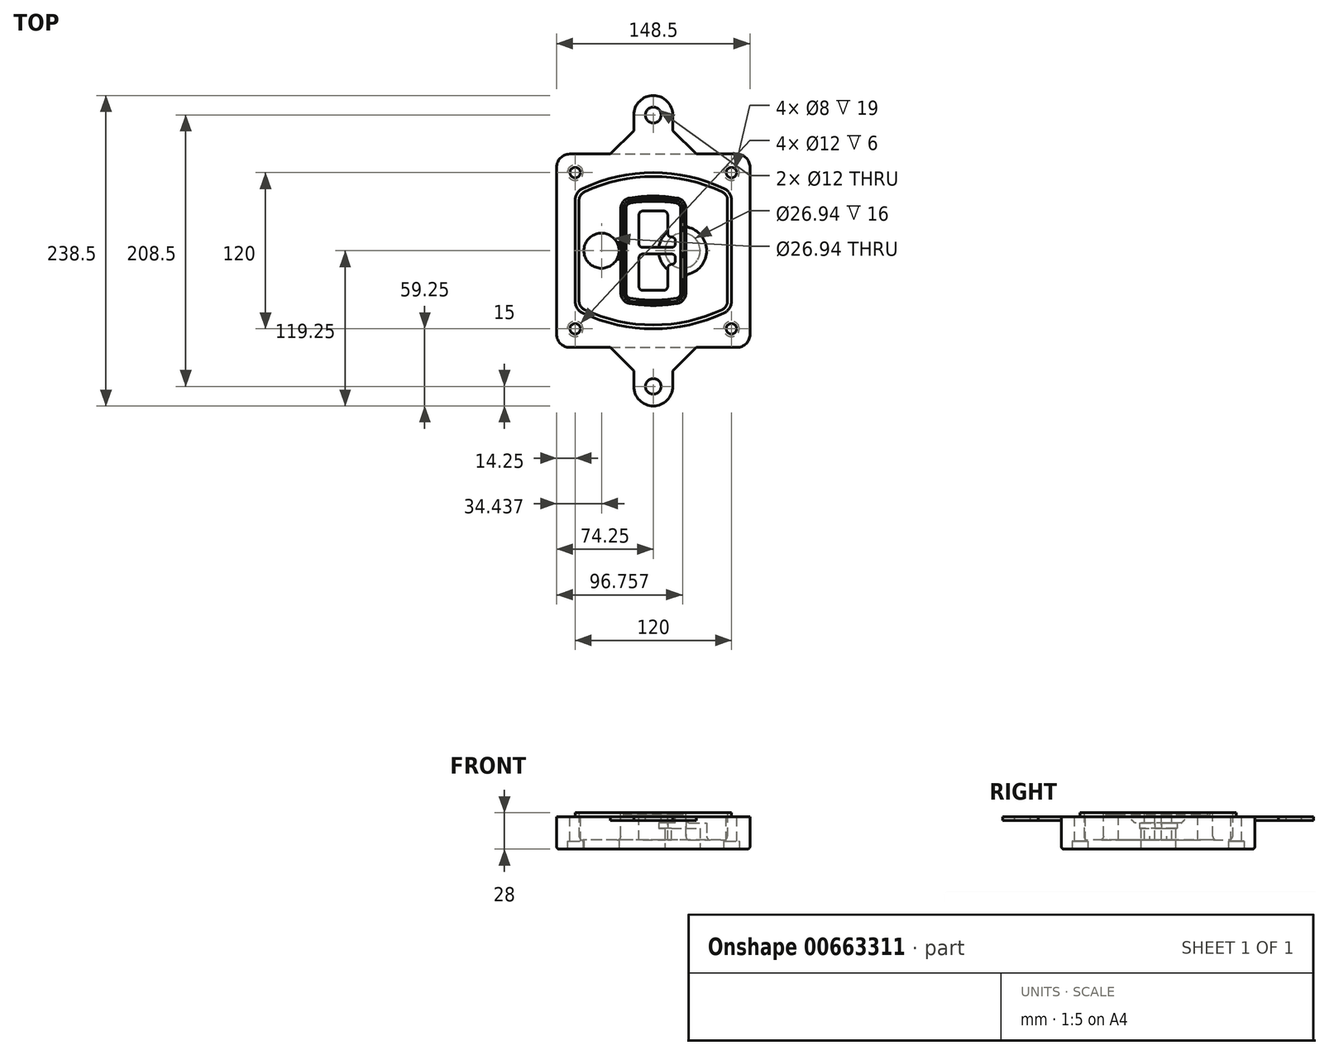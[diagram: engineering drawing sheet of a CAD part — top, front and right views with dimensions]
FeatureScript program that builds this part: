
annotation { "Feature Type Name" : "Feature", "Feature Type Description" : "" }
export const myFeature = defineFeature(function(context is Context, id is Id, definition is map)
    precondition{}
    {
        {
            var Q0;
            Q0=qCreatedBy(makeId("Top.planeOp"),FACE);
            var sketch = newSketch(context, id + "F0", { "sketchPlane" : qUnion([Q0])});
            skPoint(sketch, "E0.rect.middle", {"position": v(0, 0) * mm});
            skLineSegment(sketch, "E1.bottom", {"start": v(-64.25, -74.25) * mm, "end": v(64.25, -74.25) * mm});
            skLineSegment(sketch, "E1.top", {"start": v(-64.25, 74.25) * mm, "end": v(64.25, 74.25) * mm});
            skLineSegment(sketch, "E1.left", {"start": v(-74.25, -64.25) * mm, "end": v(-74.25, 64.25) * mm});
            skLineSegment(sketch, "E1.right", {"start": v(74.25, -64.25) * mm, "end": v(74.25, 64.25) * mm});
            skLineSegment(sketch, "E2", {"start": v(-74.25, 74.25) * mm, "end": v(74.25, -74.25) * mm, "construction": true});
            skLineSegment(sketch, "E3", {"start": v(74.25, 74.25) * mm, "end": v(-74.25, -74.25) * mm, "construction": true});
            skCircle(sketch, "E4", {"center": v(-60, 60) * mm, "radius": 4 * mm});
            skCircle(sketch, "E5", {"center": v(60, 60) * mm, "radius": 4 * mm});
            skCircle(sketch, "E6", {"center": v(60, -60) * mm, "radius": 4 * mm});
            skCircle(sketch, "E7", {"center": v(-60, -60) * mm, "radius": 4 * mm});
            skLineSegment(sketch, "E8", {"start": v(-60, 60) * mm, "end": v(60, 60) * mm, "construction": true});
            skLineSegment(sketch, "E9", {"start": v(60, 60) * mm, "end": v(60, -60) * mm, "construction": true});
            skLineSegment(sketch, "E10", {"start": v(60, -60) * mm, "end": v(-60, -60) * mm, "construction": true});
            skLineSegment(sketch, "E11", {"start": v(-60, -60) * mm, "end": v(-60, 60) * mm, "construction": true});
            skLineSegment(sketch, "E12", {"start": v(-60, 38.83) * mm, "end": v(-60, -38.83) * mm});
            skLineSegment(sketch, "E13", {"start": v(60, 38.83) * mm, "end": v(60, -38.83) * mm});
            skArc(sketch, "E14", {"start": v(54.26, 47.88) * mm, "mid": v(0, 60) * mm, "end": v(-54.26, 47.88) * mm});
            skArc(sketch, "E15", {"start": v(-54.26, -47.88) * mm, "mid": v(0, -60) * mm, "end": v(54.26, -47.88) * mm});
            skLineSegment(sketch, "E16", {"start": v(-60, 0) * mm, "end": v(60, 0) * mm, "construction": true});
            skPoint(sketch, "E17.visualSharp", {"position": v(-60, -45) * mm});
            skArc(sketch, "E17.filletArc", {"start": v(-60, -38.83) * mm, "mid": v(-58.44, -44.2) * mm, "end": v(-54.26, -47.88) * mm});
            skPoint(sketch, "E18.visualSharp", {"position": v(-60, 45) * mm});
            skArc(sketch, "E18.filletArc", {"start": v(-54.26, 47.88) * mm, "mid": v(-58.44, 44.2) * mm, "end": v(-60, 38.83) * mm});
            skPoint(sketch, "E19.visualSharp", {"position": v(60, 45) * mm});
            skArc(sketch, "E19.filletArc", {"start": v(60, 38.83) * mm, "mid": v(58.44, 44.2) * mm, "end": v(54.26, 47.88) * mm});
            skPoint(sketch, "E20.visualSharp", {"position": v(60, -45) * mm});
            skArc(sketch, "E20.filletArc", {"start": v(54.26, -47.88) * mm, "mid": v(58.44, -44.2) * mm, "end": v(60, -38.83) * mm});
            skPoint(sketch, "E21.visualSharp", {"position": v(-74.25, 74.25) * mm});
            skArc(sketch, "E21.filletArc", {"start": v(-64.25, 74.25) * mm, "mid": v(-71.32, 71.32) * mm, "end": v(-74.25, 64.25) * mm});
            skPoint(sketch, "E22.visualSharp", {"position": v(74.25, 74.25) * mm});
            skArc(sketch, "E22.filletArc", {"start": v(74.25, 64.25) * mm, "mid": v(71.32, 71.32) * mm, "end": v(64.25, 74.25) * mm});
            skPoint(sketch, "E23.visualSharp", {"position": v(74.25, -74.25) * mm});
            skArc(sketch, "E23.filletArc", {"start": v(64.25, -74.25) * mm, "mid": v(71.32, -71.32) * mm, "end": v(74.25, -64.25) * mm});
            skPoint(sketch, "E24.visualSharp", {"position": v(-74.25, -74.25) * mm});
            skArc(sketch, "E24.filletArc", {"start": v(-74.25, -64.25) * mm, "mid": v(-71.32, -71.32) * mm, "end": v(-64.25, -74.25) * mm});
            skArc(sketch, "E25.0", {"start": v(57, 38.83) * mm, "mid": v(55.9, 42.58) * mm, "end": v(52.98, 45.17) * mm});
            skLineSegment(sketch, "E25.1", {"start": v(57, 38.83) * mm, "end": v(57, -38.83) * mm});
            skArc(sketch, "E25.2", {"start": v(52.98, -45.17) * mm, "mid": v(55.9, -42.58) * mm, "end": v(57, -38.83) * mm});
            skArc(sketch, "E25.3", {"start": v(-52.98, -45.17) * mm, "mid": v(0, -57) * mm, "end": v(52.98, -45.17) * mm});
            skArc(sketch, "E25.4", {"start": v(-57, -38.83) * mm, "mid": v(-55.9, -42.58) * mm, "end": v(-52.98, -45.17) * mm});
            skArc(sketch, "E25.5", {"start": v(52.98, 45.17) * mm, "mid": v(0, 57) * mm, "end": v(-52.98, 45.17) * mm});
            skLineSegment(sketch, "E25.6", {"start": v(-57, 38.83) * mm, "end": v(-57, -38.83) * mm});
            skArc(sketch, "E25.7", {"start": v(-52.98, 45.17) * mm, "mid": v(-55.9, 42.58) * mm, "end": v(-57, 38.83) * mm});
            skArc(sketch, "E26.0", {"start": v(-55.96, 51.5) * mm, "mid": v(-61.82, 46.33) * mm, "end": v(-64, 38.83) * mm});
            skArc(sketch, "E26.1", {"start": v(55.96, 51.5) * mm, "mid": v(0, 64) * mm, "end": v(-55.96, 51.5) * mm});
            skArc(sketch, "E26.2", {"start": v(64, 38.83) * mm, "mid": v(61.82, 46.33) * mm, "end": v(55.96, 51.5) * mm});
            skLineSegment(sketch, "E26.3", {"start": v(64, 38.83) * mm, "end": v(64, -38.83) * mm});
            skArc(sketch, "E26.4", {"start": v(55.96, -51.5) * mm, "mid": v(61.82, -46.33) * mm, "end": v(64, -38.83) * mm});
            skLineSegment(sketch, "E26.5", {"start": v(-64, 38.83) * mm, "end": v(-64, -38.83) * mm});
            skArc(sketch, "E26.6", {"start": v(-55.96, -51.5) * mm, "mid": v(0, -64) * mm, "end": v(55.96, -51.5) * mm});
            skArc(sketch, "E26.7", {"start": v(-64, -38.83) * mm, "mid": v(-61.82, -46.33) * mm, "end": v(-55.96, -51.5) * mm});
            skSolve(sketch);
        }
        {
            var Q0;
            Q0=makeQuery(id+"F0.imprint","IMPRINT",FACE,{"disambiguationData":[TD([[makeQuery(id+"F0.imprint","IMPRINT",EDGE,{"derivedFrom":sQuery(id+"F0.wireOp",EDGE,"E1.bottom")}),1.0]])]});
            var Q1;
            Q1=makeQuery(id+"F0.imprint","IMPRINT",FACE,{"disambiguationData":[TD([[makeQuery(id+"F0.imprint","IMPRINT",EDGE,{"derivedFrom":sQuery(id+"F0.wireOp",EDGE,"E12")}),1.0]])]});
            var Q2;
            Q2=makeQuery(id+"F0.imprint","IMPRINT",FACE,{"disambiguationData":[TD([[makeQuery(id+"F0.imprint","IMPRINT",EDGE,{"derivedFrom":sQuery(id+"F0.wireOp",EDGE,"E25.0")}),1.0]])]});
            var Q3;
            Q3=makeQuery(id+"F0.imprint","IMPRINT",FACE,{"disambiguationData":[TD([[makeQuery(id+"F0.imprint","IMPRINT",EDGE,{"derivedFrom":sQuery(id+"F0.wireOp",EDGE,"E12")}),-1.0]])]});
            extrude(context, id + "F1", {"entities" : qUnion([Q0, Q1, Q2, Q3]), "oppositeDirection" : true, "depth" : 25 * mm});
        }
        {
            var Q0;
            Q0=makeQuery(id+"F0.imprint","IMPRINT",FACE,{"disambiguationData":[TD([[makeQuery(id+"F0.imprint","IMPRINT",EDGE,{"derivedFrom":sQuery(id+"F0.wireOp",EDGE,"E12")}),1.0]])]});
            extrude(context, id + "F2", {"entities" : qUnion([Q0]), "operationType" : NewBodyOperationType.ADD, "depth" : 3 * mm});
        }
        {
            var Q0;
            Q0=makeQuery(id+"F0.imprint","IMPRINT",FACE,{"disambiguationData":[TD([[makeQuery(id+"F0.imprint","IMPRINT",EDGE,{"derivedFrom":sQuery(id+"F0.wireOp",EDGE,"E25.0")}),1.0]])]});
            extrude(context, id + "F3", {"entities" : qUnion([Q0]), "operationType" : NewBodyOperationType.REMOVE, "oppositeDirection" : true, "depth" : 18 * mm});
        }
        {
            var Q0;
            Q0=makeQuery(id+"F2.opExtrude","CAP_FACE",FACE,{"disambiguationData":[OSD([sQuery(id+"F0.wireOp",EDGE,"E12"),sQuery(id+"F0.wireOp",EDGE,"E13"),sQuery(id+"F0.wireOp",EDGE,"E14"),sQuery(id+"F0.wireOp",EDGE,"E15"),sQuery(id+"F0.wireOp",EDGE,"E17.filletArc"),sQuery(id+"F0.wireOp",EDGE,"E18.filletArc"),sQuery(id+"F0.wireOp",EDGE,"E19.filletArc"),sQuery(id+"F0.wireOp",EDGE,"E20.filletArc"),sQuery(id+"F0.wireOp",EDGE,"E25.0"),sQuery(id+"F0.wireOp",EDGE,"E25.1"),sQuery(id+"F0.wireOp",EDGE,"E25.2"),sQuery(id+"F0.wireOp",EDGE,"E25.3"),sQuery(id+"F0.wireOp",EDGE,"E25.4"),sQuery(id+"F0.wireOp",EDGE,"E25.5"),sQuery(id+"F0.wireOp",EDGE,"E25.6"),sQuery(id+"F0.wireOp",EDGE,"E25.7")])],"isStart":false});
            var sketch = newSketch(context, id + "F4", { "sketchPlane" : qUnion([Q0])});
            skArc(sketch, "E27.0", {"start": v(-18.34, -40.45) * mm, "mid": v(0, -42) * mm, "end": v(18.34, -40.45) * mm});
            skArc(sketch, "E28.0", {"start": v(18.34, 40.45) * mm, "mid": v(0, 42) * mm, "end": v(-18.34, 40.45) * mm});
            skLineSegment(sketch, "E29", {"start": v(-25, 32.57) * mm, "end": v(-25, -32.57) * mm});
            skLineSegment(sketch, "E30", {"start": v(25, 32.57) * mm, "end": v(25, -32.57) * mm});
            skLineSegment(sketch, "E31", {"start": v(-25, 39.1) * mm, "end": v(25, 39.1) * mm, "construction": true});
            skLineSegment(sketch, "E32", {"start": v(-25, -39.1) * mm, "end": v(25, -39.1) * mm, "construction": true});
            skPoint(sketch, "E33.visualSharp", {"position": v(-25, 39.1) * mm});
            skArc(sketch, "E33.filletArc", {"start": v(-18.34, 40.45) * mm, "mid": v(-23.11, 37.73) * mm, "end": v(-25, 32.57) * mm});
            skPoint(sketch, "E34.visualSharp", {"position": v(25, 39.1) * mm});
            skArc(sketch, "E34.filletArc", {"start": v(25, 32.57) * mm, "mid": v(23.11, 37.73) * mm, "end": v(18.34, 40.45) * mm});
            skPoint(sketch, "E35.visualSharp", {"position": v(25, -39.1) * mm});
            skArc(sketch, "E35.filletArc", {"start": v(18.34, -40.45) * mm, "mid": v(23.11, -37.73) * mm, "end": v(25, -32.57) * mm});
            skPoint(sketch, "E36.visualSharp", {"position": v(-25, -39.1) * mm});
            skArc(sketch, "E36.filletArc", {"start": v(-25, -32.57) * mm, "mid": v(-23.11, -37.73) * mm, "end": v(-18.34, -40.45) * mm});
            skArc(sketch, "E37.0", {"start": v(52.98, 45.17) * mm, "mid": v(0, 57) * mm, "end": v(-52.98, 45.17) * mm});
            skArc(sketch, "E37.1", {"start": v(-52.98, 45.17) * mm, "mid": v(-55.9, 42.58) * mm, "end": v(-57, 38.83) * mm});
            skLineSegment(sketch, "E37.2", {"start": v(-57, 38.83) * mm, "end": v(-57, -38.83) * mm});
            skArc(sketch, "E37.3", {"start": v(-57, -38.83) * mm, "mid": v(-55.9, -42.58) * mm, "end": v(-52.98, -45.17) * mm});
            skArc(sketch, "E37.4", {"start": v(-52.98, -45.17) * mm, "mid": v(0, -57) * mm, "end": v(52.98, -45.17) * mm});
            skArc(sketch, "E37.5", {"start": v(52.98, -45.17) * mm, "mid": v(55.9, -42.58) * mm, "end": v(57, -38.83) * mm});
            skLineSegment(sketch, "E37.6", {"start": v(57, 38.83) * mm, "end": v(57, -38.83) * mm});
            skArc(sketch, "E37.7", {"start": v(57, 38.83) * mm, "mid": v(55.9, 42.58) * mm, "end": v(52.98, 45.17) * mm});
            skLineSegment(sketch, "E38.0", {"start": v(23, 32.57) * mm, "end": v(23, -32.57) * mm});
            skArc(sketch, "E38.1", {"start": v(18, -38.48) * mm, "mid": v(21.58, -36.44) * mm, "end": v(23, -32.57) * mm});
            skArc(sketch, "E38.2", {"start": v(-18, -38.48) * mm, "mid": v(0, -40) * mm, "end": v(18, -38.48) * mm});
            skArc(sketch, "E38.3", {"start": v(-23, -32.57) * mm, "mid": v(-21.58, -36.44) * mm, "end": v(-18, -38.48) * mm});
            skLineSegment(sketch, "E38.4", {"start": v(-23, 32.57) * mm, "end": v(-23, -32.57) * mm});
            skArc(sketch, "E38.5", {"start": v(23, 32.57) * mm, "mid": v(21.58, 36.44) * mm, "end": v(18, 38.48) * mm});
            skArc(sketch, "E38.6", {"start": v(-18, 38.48) * mm, "mid": v(-21.58, 36.44) * mm, "end": v(-23, 32.57) * mm});
            skArc(sketch, "E38.7", {"start": v(18, 38.48) * mm, "mid": v(0, 40) * mm, "end": v(-18, 38.48) * mm});
            skArc(sketch, "E39.0", {"start": v(21, 32.57) * mm, "mid": v(20.06, 35.15) * mm, "end": v(17.67, 36.5) * mm});
            skLineSegment(sketch, "E39.1", {"start": v(21, 32.57) * mm, "end": v(21, -32.57) * mm});
            skArc(sketch, "E39.2", {"start": v(17.67, -36.5) * mm, "mid": v(20.06, -35.15) * mm, "end": v(21, -32.57) * mm});
            skArc(sketch, "E39.3", {"start": v(-17.67, -36.5) * mm, "mid": v(0, -38) * mm, "end": v(17.67, -36.5) * mm});
            skArc(sketch, "E39.4", {"start": v(-21, -32.57) * mm, "mid": v(-20.06, -35.15) * mm, "end": v(-17.67, -36.5) * mm});
            skArc(sketch, "E39.5", {"start": v(17.67, 36.5) * mm, "mid": v(0, 38) * mm, "end": v(-17.67, 36.5) * mm});
            skLineSegment(sketch, "E39.6", {"start": v(-21, 32.57) * mm, "end": v(-21, -32.57) * mm});
            skArc(sketch, "E39.7", {"start": v(-17.67, 36.5) * mm, "mid": v(-20.06, 35.15) * mm, "end": v(-21, 32.57) * mm});
            skLineSegment(sketch, "E40", {"start": v(-25, 0) * mm, "end": v(25, 0) * mm, "construction": true});
            skLineSegment(sketch, "E41", {"start": v(-11, 5.5) * mm, "end": v(-11, 27.5) * mm});
            skLineSegment(sketch, "E42", {"start": v(-8, 30.5) * mm, "end": v(8, 30.5) * mm});
            skLineSegment(sketch, "E43", {"start": v(11, 27.5) * mm, "end": v(11, 13.5) * mm});
            skLineSegment(sketch, "E44", {"start": v(14, 10.5) * mm, "end": v(14, 10.5) * mm});
            skLineSegment(sketch, "E45", {"start": v(17, 7.5) * mm, "end": v(17, 5.5) * mm});
            skLineSegment(sketch, "E46", {"start": v(14, 2.5) * mm, "end": v(-8, 2.5) * mm});
            skPoint(sketch, "E47.visualSharp", {"position": v(-11, 30.5) * mm});
            skArc(sketch, "E47.filletArc", {"start": v(-8, 30.5) * mm, "mid": v(-10.12, 29.62) * mm, "end": v(-11, 27.5) * mm});
            skPoint(sketch, "E48.visualSharp", {"position": v(11, 30.5) * mm});
            skArc(sketch, "E48.filletArc", {"start": v(11, 27.5) * mm, "mid": v(10.12, 29.62) * mm, "end": v(8, 30.5) * mm});
            skPoint(sketch, "E49.visualSharp", {"position": v(11, 10.5) * mm});
            skArc(sketch, "E49.filletArc", {"start": v(11, 13.5) * mm, "mid": v(11.88, 11.38) * mm, "end": v(14, 10.5) * mm});
            skPoint(sketch, "E50.visualSharp", {"position": v(17, 10.5) * mm});
            skArc(sketch, "E50.filletArc", {"start": v(17, 7.5) * mm, "mid": v(16.12, 9.62) * mm, "end": v(14, 10.5) * mm});
            skPoint(sketch, "E51.visualSharp", {"position": v(17, 2.5) * mm});
            skArc(sketch, "E51.filletArc", {"start": v(14, 2.5) * mm, "mid": v(16.12, 3.38) * mm, "end": v(17, 5.5) * mm});
            skPoint(sketch, "E52.visualSharp", {"position": v(-11, 2.5) * mm});
            skArc(sketch, "E52.filletArc", {"start": v(-11, 5.5) * mm, "mid": v(-10.12, 3.38) * mm, "end": v(-8, 2.5) * mm});
            skLineSegment(sketch, "E53.0.MirrorCS", {"start": v(14, -2.5) * mm, "end": v(-8, -2.5) * mm});
            skArc(sketch, "E54.0.MirrorCS", {"start": v(-11, -5.5) * mm, "mid": v(-10.12, -3.38) * mm, "end": v(-8, -2.5) * mm});
            skLineSegment(sketch, "E55.0.MirrorCS", {"start": v(-11, -5.5) * mm, "end": v(-11, -27.5) * mm});
            skArc(sketch, "E56.0.MirrorCS", {"start": v(-8, -30.5) * mm, "mid": v(-10.12, -29.62) * mm, "end": v(-11, -27.5) * mm});
            skLineSegment(sketch, "E57.0.MirrorCS", {"start": v(-8, -30.5) * mm, "end": v(8, -30.5) * mm});
            skArc(sketch, "E58.0.MirrorCS", {"start": v(11, -27.5) * mm, "mid": v(10.12, -29.62) * mm, "end": v(8, -30.5) * mm});
            skLineSegment(sketch, "E59.0.MirrorCS", {"start": v(11, -27.5) * mm, "end": v(11, -13.5) * mm});
            skArc(sketch, "E60.0.MirrorCS", {"start": v(11, -13.5) * mm, "mid": v(11.88, -11.38) * mm, "end": v(14, -10.5) * mm});
            skArc(sketch, "E61.0.MirrorCS", {"start": v(17, -7.5) * mm, "mid": v(16.12, -9.62) * mm, "end": v(14, -10.5) * mm});
            skLineSegment(sketch, "E62.0.MirrorCS", {"start": v(17, -7.5) * mm, "end": v(17, -5.5) * mm});
            skArc(sketch, "E63.0.MirrorCS", {"start": v(14, -2.5) * mm, "mid": v(16.12, -3.38) * mm, "end": v(17, -5.5) * mm});
            skSolve(sketch);
        }
        {
            var Q0;
            Q0=makeQuery(id+"F4.imprint","IMPRINT",FACE,{"disambiguationData":[TD([[makeQuery(id+"F4.imprint","IMPRINT",EDGE,{"derivedFrom":sQuery(id+"F4.wireOp",EDGE,"E27.0")}),1.0]])]});
            var Q1;
            Q1=makeQuery(id+"F4.imprint","IMPRINT",FACE,{"disambiguationData":[TD([[makeQuery(id+"F4.imprint","IMPRINT",EDGE,{"derivedFrom":sQuery(id+"F4.wireOp",EDGE,"E38.0")}),-1.0]])]});
            var Q2;
            Q2=makeQuery(id+"F4.imprint","IMPRINT",FACE,{"disambiguationData":[TD([[makeQuery(id+"F4.imprint","IMPRINT",EDGE,{"derivedFrom":sQuery(id+"F4.wireOp",EDGE,"E39.0")}),1.0]])]});
            extrude(context, id + "F5", {"entities" : qUnion([Q0, Q1, Q2]), "operationType" : NewBodyOperationType.ADD, "endBound" : BoundingType.UP_TO_NEXT, "oppositeDirection" : true, "depth" : 25 * mm});
        }
        {
            var Q0;
            Q0=makeQuery(id+"F4.imprint","IMPRINT",FACE,{"disambiguationData":[TD([[makeQuery(id+"F4.imprint","IMPRINT",EDGE,{"derivedFrom":sQuery(id+"F4.wireOp",EDGE,"E38.0")}),-1.0]])]});
            extrude(context, id + "F6", {"entities" : qUnion([Q0]), "operationType" : NewBodyOperationType.REMOVE, "oppositeDirection" : true, "depth" : 2 * mm});
        }
        {
            var Q0;
            Q0=makeQuery(id+"F1.opExtrude","CAP_FACE",FACE,{"disambiguationData":[OSD([sQuery(id+"F0.wireOp",EDGE,"E1.bottom"),sQuery(id+"F0.wireOp",EDGE,"E1.top"),sQuery(id+"F0.wireOp",EDGE,"E1.left"),sQuery(id+"F0.wireOp",EDGE,"E1.right"),sQuery(id+"F0.wireOp",EDGE,"E4"),sQuery(id+"F0.wireOp",EDGE,"E5"),sQuery(id+"F0.wireOp",EDGE,"E6"),sQuery(id+"F0.wireOp",EDGE,"E7"),sQuery(id+"F0.wireOp",EDGE,"E21.filletArc"),sQuery(id+"F0.wireOp",EDGE,"E22.filletArc"),sQuery(id+"F0.wireOp",EDGE,"E23.filletArc"),sQuery(id+"F0.wireOp",EDGE,"E24.filletArc")])],"isStart":false});
            var sketch = newSketch(context, id + "F7", { "sketchPlane" : qUnion([Q0])});
            skCircle(sketch, "E64", {"center": v(22.5, 0) * mm, "radius": 13.47 * mm});
            skCircle(sketch, "E65", {"center": v(-39.81, 0) * mm, "radius": 13.47 * mm});
            skLineSegment(sketch, "E66", {"start": v(74.25, 0) * mm, "end": v(-74.25, 0) * mm});
            skCircle(sketch, "E67", {"center": v(22.5, 0) * mm, "radius": 18.47 * mm});
            skCircle(sketch, "E68", {"center": v(60, -60) * mm, "radius": 6 * mm});
            skCircle(sketch, "E69", {"center": v(-60, -60) * mm, "radius": 6 * mm});
            skCircle(sketch, "E70", {"center": v(-60, 60) * mm, "radius": 6 * mm});
            skCircle(sketch, "E71", {"center": v(60, 60) * mm, "radius": 6 * mm});
            skSolve(sketch);
        }
        {
            var Q0;
            {var subQ1=sQuery(id+"F7.wireOp",EDGE,"E66");var subQ4=sQuery(id+"F7.wireOp",EDGE,"E64");var subQ6=makeQuery(id+"F7.imprint","INTERSECT",VERTEX,{"disambiguationData":[OD(0.0)],"derivedFrom":[subQ4,subQ1]});Q0=makeQuery(id+"F7.imprint","IMPRINT",FACE,{"disambiguationData":[TD([[makeQuery(id+"F7.imprint","IMPRINT",EDGE,{"disambiguationData":[TD([[subQ6,-1.0]])],"derivedFrom":subQ4}),-1.0]])]});}
            var Q1;
            {var subQ0=sQuery(id+"F7.wireOp",EDGE,"E66");var subQ1=sQuery(id+"F7.wireOp",EDGE,"E64");var subQ3=makeQuery(id+"F7.imprint","INTERSECT",VERTEX,{"disambiguationData":[OD(0.0)],"derivedFrom":[subQ1,subQ0]});Q1=makeQuery(id+"F7.imprint","IMPRINT",FACE,{"disambiguationData":[TD([[makeQuery(id+"F7.imprint","IMPRINT",EDGE,{"disambiguationData":[TD([[subQ3,-1.0]])],"derivedFrom":subQ1}),1.0]])]});}
            var Q2;
            {var subQ0=sQuery(id+"F7.wireOp",EDGE,"E66");var subQ1=sQuery(id+"F7.wireOp",EDGE,"E64");var subQ3=makeQuery(id+"F7.imprint","INTERSECT",VERTEX,{"disambiguationData":[OD(0.0)],"derivedFrom":[subQ1,subQ0]});Q2=makeQuery(id+"F7.imprint","IMPRINT",FACE,{"disambiguationData":[TD([[makeQuery(id+"F7.imprint","IMPRINT",EDGE,{"disambiguationData":[TD([[subQ3,1.0]])],"derivedFrom":subQ1}),1.0]])]});}
            var Q3;
            {var subQ1=sQuery(id+"F7.wireOp",EDGE,"E66");var subQ4=sQuery(id+"F7.wireOp",EDGE,"E64");var subQ6=makeQuery(id+"F7.imprint","INTERSECT",VERTEX,{"disambiguationData":[OD(0.0)],"derivedFrom":[subQ4,subQ1]});Q3=makeQuery(id+"F7.imprint","IMPRINT",FACE,{"disambiguationData":[TD([[makeQuery(id+"F7.imprint","IMPRINT",EDGE,{"disambiguationData":[TD([[subQ6,1.0]])],"derivedFrom":subQ4}),-1.0]])]});}
            extrude(context, id + "F8", {"entities" : qUnion([Q0, Q1, Q2, Q3]), "operationType" : NewBodyOperationType.ADD, "oppositeDirection" : true, "depth" : 20 * mm});
        }
        {
            var Q0;
            {var subQ0=sQuery(id+"F7.wireOp",EDGE,"E66");var subQ1=sQuery(id+"F7.wireOp",EDGE,"E64");var subQ3=makeQuery(id+"F7.imprint","INTERSECT",VERTEX,{"disambiguationData":[OD(0.0)],"derivedFrom":[subQ1,subQ0]});Q0=makeQuery(id+"F7.imprint","IMPRINT",FACE,{"disambiguationData":[TD([[makeQuery(id+"F7.imprint","IMPRINT",EDGE,{"disambiguationData":[TD([[subQ3,-1.0]])],"derivedFrom":subQ1}),1.0]])]});}
            var Q1;
            {var subQ0=sQuery(id+"F7.wireOp",EDGE,"E66");var subQ1=sQuery(id+"F7.wireOp",EDGE,"E64");var subQ3=makeQuery(id+"F7.imprint","INTERSECT",VERTEX,{"disambiguationData":[OD(0.0)],"derivedFrom":[subQ1,subQ0]});Q1=makeQuery(id+"F7.imprint","IMPRINT",FACE,{"disambiguationData":[TD([[makeQuery(id+"F7.imprint","IMPRINT",EDGE,{"disambiguationData":[TD([[subQ3,1.0]])],"derivedFrom":subQ1}),1.0]])]});}
            extrude(context, id + "F9", {"entities" : qUnion([Q0, Q1]), "operationType" : NewBodyOperationType.REMOVE, "oppositeDirection" : true, "depth" : 16 * mm});
        }
        {
            var Q0;
            {var subQ0=sQuery(id+"F7.wireOp",EDGE,"E66");var subQ1=sQuery(id+"F7.wireOp",EDGE,"E65");var subQ3=makeQuery(id+"F7.imprint","INTERSECT",VERTEX,{"disambiguationData":[OD(0.0)],"derivedFrom":[subQ1,subQ0]});Q0=makeQuery(id+"F7.imprint","IMPRINT",FACE,{"disambiguationData":[TD([[makeQuery(id+"F7.imprint","IMPRINT",EDGE,{"disambiguationData":[TD([[subQ3,-1.0]])],"derivedFrom":subQ1}),1.0]])]});}
            var Q1;
            {var subQ0=sQuery(id+"F7.wireOp",EDGE,"E66");var subQ1=sQuery(id+"F7.wireOp",EDGE,"E65");var subQ3=makeQuery(id+"F7.imprint","INTERSECT",VERTEX,{"disambiguationData":[OD(0.0)],"derivedFrom":[subQ1,subQ0]});Q1=makeQuery(id+"F7.imprint","IMPRINT",FACE,{"disambiguationData":[TD([[makeQuery(id+"F7.imprint","IMPRINT",EDGE,{"disambiguationData":[TD([[subQ3,1.0]])],"derivedFrom":subQ1}),1.0]])]});}
            extrude(context, id + "F10", {"entities" : qUnion([Q0, Q1]), "operationType" : NewBodyOperationType.REMOVE, "oppositeDirection" : true, "depth" : 25 * mm});
        }
        {
            var Q0;
            Q0=makeQuery(id+"F7.imprint","IMPRINT",FACE,{"disambiguationData":[TD([[makeQuery(id+"F7.imprint","IMPRINT",EDGE,{"derivedFrom":sQuery(id+"F7.wireOp",EDGE,"E68")}),1.0]])]});
            var Q1;
            Q1=makeQuery(id+"F7.imprint","IMPRINT",FACE,{"disambiguationData":[TD([[makeQuery(id+"F7.imprint","IMPRINT",EDGE,{"derivedFrom":makeQuery(id+"F1.opExtrude","CAP_EDGE",EDGE,{"disambiguationData":[OSD([sQuery(id+"F0.wireOp",EDGE,"E5")])],"isStart":false})}),-1.0]])]});
            var Q2;
            Q2=makeQuery(id+"F7.imprint","IMPRINT",FACE,{"disambiguationData":[TD([[makeQuery(id+"F7.imprint","IMPRINT",EDGE,{"derivedFrom":sQuery(id+"F7.wireOp",EDGE,"E69")}),1.0]])]});
            var Q3;
            Q3=makeQuery(id+"F7.imprint","IMPRINT",FACE,{"disambiguationData":[TD([[makeQuery(id+"F7.imprint","IMPRINT",EDGE,{"derivedFrom":makeQuery(id+"F1.opExtrude","CAP_EDGE",EDGE,{"disambiguationData":[OSD([sQuery(id+"F0.wireOp",EDGE,"E4")])],"isStart":false})}),-1.0]])]});
            var Q4;
            Q4=makeQuery(id+"F7.imprint","IMPRINT",FACE,{"disambiguationData":[TD([[makeQuery(id+"F7.imprint","IMPRINT",EDGE,{"derivedFrom":sQuery(id+"F7.wireOp",EDGE,"E70")}),1.0]])]});
            var Q5;
            Q5=makeQuery(id+"F7.imprint","IMPRINT",FACE,{"disambiguationData":[TD([[makeQuery(id+"F7.imprint","IMPRINT",EDGE,{"derivedFrom":makeQuery(id+"F1.opExtrude","CAP_EDGE",EDGE,{"disambiguationData":[OSD([sQuery(id+"F0.wireOp",EDGE,"E7")])],"isStart":false})}),-1.0]])]});
            var Q6;
            Q6=makeQuery(id+"F7.imprint","IMPRINT",FACE,{"disambiguationData":[TD([[makeQuery(id+"F7.imprint","IMPRINT",EDGE,{"derivedFrom":sQuery(id+"F7.wireOp",EDGE,"E71")}),1.0]])]});
            var Q7;
            Q7=makeQuery(id+"F7.imprint","IMPRINT",FACE,{"disambiguationData":[TD([[makeQuery(id+"F7.imprint","IMPRINT",EDGE,{"derivedFrom":makeQuery(id+"F1.opExtrude","CAP_EDGE",EDGE,{"disambiguationData":[OSD([sQuery(id+"F0.wireOp",EDGE,"E6")])],"isStart":false})}),-1.0]])]});
            extrude(context, id + "F11", {"entities" : qUnion([Q0, Q1, Q2, Q3, Q4, Q5, Q6, Q7]), "operationType" : NewBodyOperationType.REMOVE, "oppositeDirection" : true, "depth" : 6 * mm});
        }
        {
            var Q0;
            Q0=makeQuery(id+"F9.boolean.opBoolean","COPY",FACE,{"derivedFrom":makeQuery(id+"F9.opExtrude","CAP_FACE",FACE,{"disambiguationData":[OSD([sQuery(id+"F7.wireOp",EDGE,"E64")])],"isStart":false})});
            var sketch = newSketch(context, id + "F12", { "sketchPlane" : qUnion([Q0])});
            skArc(sketch, "E72.0", {"start": v(11, 14.45) * mm, "mid": v(6.45, 9.13) * mm, "end": v(4.2, 2.5) * mm});
            skArc(sketch, "E72.1", {"start": v(4.2, -2.5) * mm, "mid": v(6.45, -9.13) * mm, "end": v(11, -14.45) * mm});
            skLineSegment(sketch, "E73", {"start": v(4.2, -2.5) * mm, "end": v(14, -2.5) * mm});
            skLineSegment(sketch, "E74.0", {"start": v(14, 2.5) * mm, "end": v(4.2, 2.5) * mm});
            skArc(sketch, "E74.1", {"start": v(14, 2.5) * mm, "mid": v(16.12, 3.38) * mm, "end": v(17, 5.5) * mm});
            skLineSegment(sketch, "E74.2", {"start": v(17, 7.5) * mm, "end": v(17, 5.5) * mm});
            skArc(sketch, "E74.3", {"start": v(17, 7.5) * mm, "mid": v(16.12, 9.62) * mm, "end": v(14, 10.5) * mm});
            skArc(sketch, "E74.4", {"start": v(11, 13.5) * mm, "mid": v(11.88, 11.38) * mm, "end": v(14, 10.5) * mm});
            skLineSegment(sketch, "E74.5", {"start": v(11, 14.45) * mm, "end": v(11, 13.5) * mm});
            skLineSegment(sketch, "E74.7", {"start": v(14, -2.5) * mm, "end": v(4.2, -2.5) * mm});
            skArc(sketch, "E74.8", {"start": v(14, -2.5) * mm, "mid": v(16.12, -3.38) * mm, "end": v(17, -5.5) * mm});
            skLineSegment(sketch, "E74.9", {"start": v(17, -7.5) * mm, "end": v(17, -5.5) * mm});
            skArc(sketch, "E74.10", {"start": v(17, -7.5) * mm, "mid": v(16.12, -9.62) * mm, "end": v(14, -10.5) * mm});
            skArc(sketch, "E74.11", {"start": v(11, -13.5) * mm, "mid": v(11.88, -11.38) * mm, "end": v(14, -10.5) * mm});
            skLineSegment(sketch, "E74.12", {"start": v(11, -14.45) * mm, "end": v(11, -13.5) * mm});
            skPoint(sketch, "E75.orphan", {"position": v(11, -27.5) * mm});
            skPoint(sketch, "E76.orphan", {"position": v(-8, -2.5) * mm});
            skPoint(sketch, "E77.orphan", {"position": v(-8, 2.5) * mm});
            skPoint(sketch, "E78.orphan", {"position": v(11, 27.5) * mm});
            skSolve(sketch);
        }
        {
            var Q0;
            {var subQ7=sQuery(id+"F12.wireOp",EDGE,"E72.0");var subQ14=sQuery(id+"F12.wireOp",EDGE,"E72.1");var subQ16=sQuery(id+"F12.wireOp",EDGE,"E74.1");var subQ18=sQuery(id+"F12.wireOp",EDGE,"E74.8");Q0=qUnion([makeQuery(id+"F12.imprint","IMPRINT",FACE,{"disambiguationData":[TD([[makeQuery(id+"F12.imprint","IMPRINT",EDGE,{"derivedFrom":subQ7}),1.0]])]}),makeQuery(id+"F12.imprint","IMPRINT",FACE,{"disambiguationData":[TD([[makeQuery(id+"F12.imprint","IMPRINT",EDGE,{"derivedFrom":subQ14}),1.0]])]}),makeQuery(id+"F12.imprint","IMPRINT",FACE,{"disambiguationData":[TD([[makeQuery(id+"F12.imprint","IMPRINT",EDGE,{"derivedFrom":subQ16}),1.0]])]}),makeQuery(id+"F12.imprint","IMPRINT",FACE,{"disambiguationData":[TD([[makeQuery(id+"F12.imprint","IMPRINT",EDGE,{"derivedFrom":subQ18}),-1.0]])]})]);}
            var Q1;
            Q1=makeQuery(id+"F5.boolean.opBoolean","SPLIT",FACE,{"disambiguationData":[TD([makeQuery(id+"F5.opExtrude","SWEPT_FACE",FACE,{"disambiguationData":[OSD([sQuery(id+"F4.wireOp",EDGE,"E41")])]})])],"derivedFrom":makeQuery(id+"F3.boolean.opBoolean","COPY",FACE,{"derivedFrom":makeQuery(id+"F3.opExtrude","CAP_FACE",FACE,{"disambiguationData":[OSD([sQuery(id+"F0.wireOp",EDGE,"E25.0"),sQuery(id+"F0.wireOp",EDGE,"E25.1"),sQuery(id+"F0.wireOp",EDGE,"E25.2"),sQuery(id+"F0.wireOp",EDGE,"E25.3"),sQuery(id+"F0.wireOp",EDGE,"E25.4"),sQuery(id+"F0.wireOp",EDGE,"E25.5"),sQuery(id+"F0.wireOp",EDGE,"E25.6"),sQuery(id+"F0.wireOp",EDGE,"E25.7")])],"isStart":false})})});
            extrude(context, id + "F13", {"entities" : qUnion([Q0]), "operationType" : NewBodyOperationType.REMOVE, "endBound" : BoundingType.UP_TO_SURFACE, "endBoundEntityFace" : qUnion([Q1]), "depth" : 25 * mm});
        }
        {
            var Q0;
            Q0=makeQuery(id+"F3.boolean.opBoolean","COPY",EDGE,{"derivedFrom":makeQuery(id+"F3.opExtrude","CAP_EDGE",EDGE,{"disambiguationData":[OSD([sQuery(id+"F0.wireOp",EDGE,"E25.6")])],"isStart":false})});
            var Q1;
            Q1=makeQuery(id+"F8.boolean.opBoolean","INTERSECT",EDGE,{"derivedFrom":[makeQuery(id+"F5.opExtrude","SWEPT_FACE",FACE,{"disambiguationData":[OSD([sQuery(id+"F4.wireOp",EDGE,"E30")])]}),makeQuery(id+"F8.opExtrude","CAP_FACE",FACE,{"disambiguationData":[OSD([sQuery(id+"F7.wireOp",EDGE,"E67")])],"isStart":false})]});
            var Q2;
            Q2=makeQuery(id+"F8.boolean.opBoolean","INTERSECT",EDGE,{"disambiguationData":[OD(1.0)],"derivedFrom":[makeQuery(id+"F5.opExtrude","SWEPT_FACE",FACE,{"disambiguationData":[OSD([sQuery(id+"F4.wireOp",EDGE,"E30")])]}),makeQuery(id+"F8.opExtrude","SWEPT_FACE",FACE,{"disambiguationData":[OSD([sQuery(id+"F7.wireOp",EDGE,"E67")])]})]});
            var Q3;
            {var subQ0=sQuery(id+"F4.wireOp",EDGE,"E30");Q3=makeQuery(id+"F8.boolean.opBoolean","SPLIT",EDGE,{"disambiguationData":[TD([makeQuery(id+"F5.opExtrude","SWEPT_FACE",FACE,{"disambiguationData":[OSD([sQuery(id+"F4.wireOp",EDGE,"E35.filletArc")])]})])],"derivedFrom":makeQuery(id+"F5.opExtrude","CAP_EDGE",EDGE,{"disambiguationData":[OSD([subQ0])],"isStart":false})});}
            var Q4;
            {var subQ0=sQuery(id+"F0.wireOp",EDGE,"E25.7");var subQ1=sQuery(id+"F0.wireOp",EDGE,"E25.1");var subQ2=sQuery(id+"F0.wireOp",EDGE,"E25.6");var subQ3=sQuery(id+"F0.wireOp",EDGE,"E25.5");var subQ4=sQuery(id+"F0.wireOp",EDGE,"E25.4");var subQ5=sQuery(id+"F0.wireOp",EDGE,"E25.0");var subQ6=sQuery(id+"F0.wireOp",EDGE,"E25.2");var subQ7=sQuery(id+"F0.wireOp",EDGE,"E25.3");Q4=makeQuery(id+"F8.boolean.opBoolean","INTERSECT",EDGE,{"derivedFrom":[makeQuery(id+"F5.boolean.opBoolean","SPLIT",FACE,{"disambiguationData":[TD([makeQuery(id+"F2.opExtrude","SWEPT_FACE",FACE,{"disambiguationData":[OSD([subQ5])]})])],"derivedFrom":makeQuery(id+"F3.boolean.opBoolean","COPY",FACE,{"derivedFrom":makeQuery(id+"F3.opExtrude","CAP_FACE",FACE,{"disambiguationData":[OSD([subQ5,subQ1,subQ6,subQ7,subQ4,subQ3,subQ2,subQ0])],"isStart":false})})}),makeQuery(id+"F8.opExtrude","SWEPT_FACE",FACE,{"disambiguationData":[OSD([sQuery(id+"F7.wireOp",EDGE,"E67")])]})]});}
            var Q5;
            Q5=makeQuery(id+"F8.boolean.opBoolean","INTERSECT",EDGE,{"disambiguationData":[OD(0.0)],"derivedFrom":[makeQuery(id+"F5.opExtrude","SWEPT_FACE",FACE,{"disambiguationData":[OSD([sQuery(id+"F4.wireOp",EDGE,"E30")])]}),makeQuery(id+"F8.opExtrude","SWEPT_FACE",FACE,{"disambiguationData":[OSD([sQuery(id+"F7.wireOp",EDGE,"E67")])]})]});
            fillet(context, id + "F14", {"entities" : qUnion([Q0, Q1, Q2, Q3, Q4, Q5]), "radius" : 3 * mm, "tangentPropagation" : true, "allowEdgeOverflow" : false});
        }
        {
            var Q0;
            Q0=makeQuery(id+"F1.opExtrude","CAP_EDGE",EDGE,{"disambiguationData":[OSD([sQuery(id+"F0.wireOp",EDGE,"E1.bottom")])],"isStart":false});
            fillet(context, id + "F15", {"entities" : qUnion([Q0]), "radius" : 2 * mm, "tangentPropagation" : true, "allowEdgeOverflow" : false});
        }
        {
            var Q0;
            {var subQ0=sQuery(id+"F0.wireOp",EDGE,"E21.filletArc");var subQ1=sQuery(id+"F0.wireOp",EDGE,"E7");var subQ2=sQuery(id+"F0.wireOp",EDGE,"E6");var subQ3=sQuery(id+"F0.wireOp",EDGE,"E5");var subQ4=sQuery(id+"F0.wireOp",EDGE,"E4");var subQ5=sQuery(id+"F0.wireOp",EDGE,"E22.filletArc");var subQ6=sQuery(id+"F0.wireOp",EDGE,"E1.bottom");var subQ7=sQuery(id+"F0.wireOp",EDGE,"E1.right");var subQ8=sQuery(id+"F0.wireOp",EDGE,"E1.top");var subQ9=sQuery(id+"F0.wireOp",EDGE,"E1.left");var subQ10=sQuery(id+"F0.wireOp",EDGE,"E23.filletArc");var subQ11=sQuery(id+"F0.wireOp",EDGE,"E24.filletArc");Q0=makeQuery(id+"F2.boolean.opBoolean","SPLIT",FACE,{"disambiguationData":[TD([makeQuery(id+"F1.opExtrude","SWEPT_FACE",FACE,{"disambiguationData":[OSD([subQ6])]})])],"derivedFrom":makeQuery(id+"F1.opExtrude","CAP_FACE",FACE,{"disambiguationData":[OSD([subQ6,subQ8,subQ9,subQ7,subQ4,subQ3,subQ2,subQ1,subQ0,subQ5,subQ10,subQ11])],"isStart":true})});}
            var sketch = newSketch(context, id + "F16", { "sketchPlane" : qUnion([Q0])});
            skLineSegment(sketch, "E79", {"start": v(-81.56, 0) * mm, "end": v(77.84, 0) * mm, "construction": true});
            skPoint(sketch, "E79.startSnap0", {"position": v(-74.25, 0) * mm});
            skSolve(sketch);
        }
        {
            var Q0;
            Q0=qCreatedBy(makeId("Top.planeOp"),FACE);
            var sketch = newSketch(context, id + "F17", { "sketchPlane" : qUnion([Q0])});
            skLineSegment(sketch, "E80", {"start": v(0, 0) * mm, "end": v(0, 165.1) * mm, "construction": true});
            skPoint(sketch, "E81", {"position": v(0, 104.25) * mm});
            skCircle(sketch, "E82", {"center": v(0, 104.25) * mm, "radius": 6 * mm});
            skArc(sketch, "E83", {"start": v(15, 104.25) * mm, "mid": v(0, 119.25) * mm, "end": v(-15, 104.25) * mm});
            skLineSegment(sketch, "E84", {"start": v(-15, 104.25) * mm, "end": v(-15, 92.25) * mm});
            skLineSegment(sketch, "E85.MirrorCS", {"start": v(15, 104.25) * mm, "end": v(15, 92.25) * mm});
            skLineSegment(sketch, "E86", {"start": v(-15, 92.25) * mm, "end": v(-33, 74.25) * mm});
            skPoint(sketch, "E87.orphan", {"position": v(-15, 80.25) * mm});
            skPoint(sketch, "E88.orphan", {"position": v(15, 80.25) * mm});
            skLineSegment(sketch, "E89.0", {"start": v(-64.25, 74.25) * mm, "end": v(64.25, 74.25) * mm});
            skLineSegment(sketch, "E90.MirrorCS", {"start": v(15, 92.25) * mm, "end": v(33, 74.25) * mm});
            skArc(sketch, "E91.MirrorCS", {"start": v(15, -104.25) * mm, "mid": v(0, -119.25) * mm, "end": v(-15, -104.25) * mm});
            skLineSegment(sketch, "E92.MirrorCS", {"start": v(-15, -104.25) * mm, "end": v(-15, -92.25) * mm});
            skLineSegment(sketch, "E93.MirrorCS", {"start": v(-15, -92.25) * mm, "end": v(-33, -74.25) * mm});
            skLineSegment(sketch, "E94.MirrorCS", {"start": v(15, -104.25) * mm, "end": v(15, -92.25) * mm});
            skLineSegment(sketch, "E95.MirrorCS", {"start": v(15, -92.25) * mm, "end": v(33, -74.25) * mm});
            skCircle(sketch, "E96.MirrorC", {"center": v(0, -104.25) * mm, "radius": 6 * mm});
            skSolve(sketch);
        }
        {
            var Q0;
            Q0=makeQuery(id+"F17.imprint","IMPRINT",FACE,{"disambiguationData":[TD([[makeQuery(id+"F17.imprint","IMPRINT",EDGE,{"derivedFrom":sQuery(id+"F17.wireOp",EDGE,"E83")}),1.0]])]});
            extrude(context, id + "F18", {"entities" : qUnion([Q0]), "oppositeDirection" : true, "depth" : 3 * mm, "offsetDistance" : 25 * mm});
        }
        {
            var Q0;
            Q0=makeQuery(id+"F17.imprint","IMPRINT",FACE,{"disambiguationData":[TD([[makeQuery(id+"F17.imprint","IMPRINT",EDGE,{"derivedFrom":sQuery(id+"F17.wireOp",EDGE,"E83")}),1.0]])]});
            extrude(context, id + "F19", {"entities" : qUnion([Q0]), "oppositeDirection" : true, "depth" : 3 * mm, "offsetDistance" : 25 * mm});
        }
        {
            var Q0;
            Q0=makeQuery(id+"F18.opExtrude","SWEPT_BODY",BODY,{"disambiguationData":[OSD([sQuery(id+"F17.wireOp",EDGE,"E83"),sQuery(id+"F17.wireOp",EDGE,"E84"),sQuery(id+"F17.wireOp",EDGE,"E85.MirrorCS"),sQuery(id+"F17.wireOp",EDGE,"E86"),sQuery(id+"F17.wireOp",EDGE,"E89.0"),sQuery(id+"F17.wireOp",EDGE,"E90.MirrorCS"),sQuery(id+"F17.wireOp",EDGE,"E82")])]});
            var Q1;
            Q1=qCreatedBy(makeId("Front.planeOp"),FACE);
            mirror(context, id + "F20", {"operationType" : NewBodyOperationType.ADD, "entities" : qUnion([Q0]), "mirrorPlane" : qUnion([Q1])});
        }
    });
